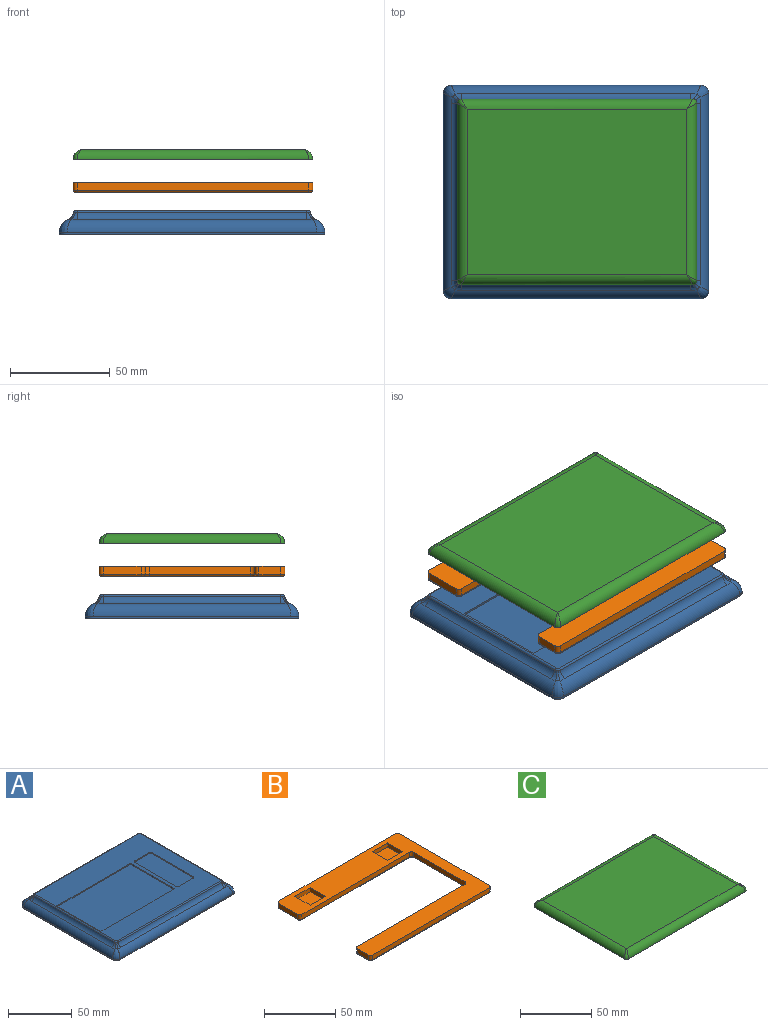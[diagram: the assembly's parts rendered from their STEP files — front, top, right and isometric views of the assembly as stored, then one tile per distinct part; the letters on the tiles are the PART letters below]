
ASSEMBLY  parts=3 mates=2
PART A: 56 faces, bbox 133x107x12 mm
  f0: plane 117x91mm, normal (0,0,1), area 5700.6mm2, adj f18,f19,f20,f21,f22,f23,f24,f25
  f1: plane 125x1mm, normal (0,1,0), area 125mm2, adj f5,f6,f9,f10
  f2: plane 99x1mm, normal (-1,0,0), area 99mm2, adj f5,f6,f7,f13
  f3: plane 125x1mm, normal (0,-1,0), area 125mm2, adj f5,f7,f8,f17
  f4: plane 99x1mm, normal (1,0,0), area 99mm2, adj f5,f8,f9,f14
  f5: plane 133x107mm, normal (0,0,-1), area 14217.3mm2, adj f1,f2,f3,f4,f6,f7,f8,f9
  f6: cylinder r=4mm len=4mm, axis (0,0,1), area 6.3mm2, adj f1,f2,f5,f11
  f7: cylinder r=4mm len=4mm, axis (0,0,-1), area 6.3mm2, adj f2,f3,f5,f15
  f8: cylinder r=4mm len=4mm, axis (0,0,1), area 6.3mm2, adj f3,f4,f5,f16
  f9: cylinder r=4mm len=4mm, axis (0,0,-1), area 6.3mm2, adj f1,f4,f5,f12
  f10: cylinder r=7mm len=125mm, axis (1,0,0), area 991mm2, adj f1,f11,f12,f39,f40,f41
  f11: bspline ~7.26x6.22mm, area 43.4mm2, adj f6,f10,f13,f37
  f12: bspline ~7.26x6.22mm, area 43.4mm2, adj f9,f10,f14,f38
  f13: cylinder r=7mm len=99mm, axis (0,1,0), area 782.1mm2, adj f2,f11,f15,f31,f33,f35
  f14: cylinder r=7mm len=99mm, axis (0,-1,0), area 782.1mm2, adj f4,f12,f16,f32,f34,f36
  f15: bspline ~7.26x6.22mm, area 43.4mm2, adj f7,f13,f17,f29
  f16: bspline ~7.26x6.22mm, area 43.4mm2, adj f8,f14,f17,f30
  f17: cylinder r=7mm len=125mm, axis (-1,0,0), area 991mm2, adj f3,f15,f16,f26,f27,f28
  f18: cylinder r=1mm len=115mm, axis (-1,0,0), area 162.5mm2, adj f0,f19,f20,f26
  f19: torus R=1mm, axis (0,0,1), area 3.4mm2, adj f0,f18,f21,f27,f29,f31
  f20: torus R=1mm, axis (0,0,1), area 3.4mm2, adj f0,f18,f22,f28,f30,f32
  f21: cylinder r=1mm len=89mm, axis (0,1,0), area 125.8mm2, adj f0,f19,f23,f33
  f22: cylinder r=1mm len=89mm, axis (0,-1,0), area 125.8mm2, adj f0,f20,f24,f34
  f23: torus R=1mm, axis (0,0,1), area 3.4mm2, adj f0,f21,f25,f35,f37,f39
  f24: torus R=1mm, axis (0,0,1), area 3.4mm2, adj f0,f22,f25,f36,f38,f40
  f25: cylinder r=1mm len=115mm, axis (1,0,0), area 162.5mm2, adj f0,f23,f24,f41
  f26: cylinder r=5mm len=115mm, axis (-1,0,0), area 569.3mm2, adj f17,f18,f27,f28
  f27: bspline ~5.33x3.88mm, area 9.5mm2, adj f17,f19,f26,f29
  f28: bspline ~5.12x3.85mm, area 9.5mm2, adj f17,f20,f26,f30
  f29: bspline ~3.88x3.85mm, area 7.1mm2, adj f15,f19,f27,f31
  f30: bspline ~3.9x3.82mm, area 7.1mm2, adj f16,f20,f28,f32
  f31: bspline ~5.33x3.88mm, area 9.5mm2, adj f13,f19,f29,f33
  f32: bspline ~5.33x3.88mm, area 9.5mm2, adj f14,f20,f30,f34
  f33: cylinder r=5mm len=89mm, axis (0,1,0), area 440.6mm2, adj f13,f21,f31,f35
  f34: cylinder r=5mm len=89mm, axis (0,1,0), area 440.6mm2, adj f14,f22,f32,f36
  f35: bspline ~5.33x3.88mm, area 9.5mm2, adj f13,f23,f33,f37
  f36: bspline ~5.12x3.85mm, area 9.5mm2, adj f14,f24,f34,f38
  f37: bspline ~3.9x3.82mm, area 7.1mm2, adj f11,f23,f35,f39
  f38: bspline ~3.88x3.85mm, area 7.1mm2, adj f12,f24,f36,f40
  f39: bspline ~5.33x3.88mm, area 9.5mm2, adj f10,f23,f37,f41
  f40: bspline ~5.33x3.88mm, area 9.5mm2, adj f10,f24,f38,f41
  f41: cylinder r=5mm len=115mm, axis (-1,0,0), area 569.3mm2, adj f10,f25,f39,f40
  f42: plane 45x1mm, normal (-1,0,0), area 45mm2, adj f0,f43,f49,f50
  f43: cylinder r=2mm len=2mm, axis (0,0,1), area 3.1mm2, adj f0,f42,f44,f50
  f44: plane 15x1mm, normal (0,-1,0), area 15mm2, adj f0,f43,f45,f50
  f45: cylinder r=2mm len=2mm, axis (0,0,1), area 3.1mm2, adj f0,f44,f46,f50
  f46: plane 45x1mm, normal (1,0,0), area 45mm2, adj f0,f45,f47,f50
  f47: cylinder r=2mm len=2mm, axis (0,0,1), area 3.1mm2, adj f0,f46,f48,f50
  f48: plane 15x1mm, normal (0,1,0), area 15mm2, adj f0,f47,f49,f50
  f49: cylinder r=2mm len=2mm, axis (0,0,1), area 3.1mm2, adj f0,f42,f48,f50
  f50: plane 49x19mm, normal (0,0,1), area 927.6mm2, adj f42,f43,f44,f45,f46,f47,f48,f49
  f51: plane 82x1mm, normal (0,-1,0), area 82mm2, adj f0,f52,f54,f55
  f52: plane 49x1mm, normal (1,0,0), area 49mm2, adj f0,f51,f53,f55
  f53: plane 82x1mm, normal (0,1,0), area 82mm2, adj f0,f52,f54,f55
  f54: plane 49x1mm, normal (-1,0,0), area 49mm2, adj f0,f51,f53,f55
  f55: plane 82x49mm, normal (0,0,1), area 4018mm2, adj f51,f52,f53,f54
PART B: 44 faces, bbox 120.3x93.3x5 mm
  f0: plane 120x93mm, normal (0,0,1), area 4601.6mm2, adj f1,f2,f3,f4,f5,f6,f7,f8
  f1: cylinder r=2mm len=4mm, axis (0,0,-1), area 12.6mm2, adj f0,f2,f16,f42
  f2: plane 51x4mm, normal (-1,0,0), area 204mm2, adj f0,f1,f3,f40
  f3: cylinder r=2mm len=4mm, axis (0,0,-1), area 12.6mm2, adj f0,f2,f4,f38
  f4: plane 107x4mm, normal (0,1,0), area 428mm2, adj f0,f3,f5,f36
  f5: cylinder r=2mm len=4mm, axis (0,0,-1), area 12.6mm2, adj f0,f4,f6,f34
  f6: plane 11x4mm, normal (-1,0,0), area 44mm2, adj f0,f5,f7,f32
  f7: cylinder r=2mm len=4mm, axis (0,0,-1), area 12.6mm2, adj f0,f6,f8,f30
  f8: plane 116x4mm, normal (0,-1,0), area 464mm2, adj f0,f7,f9,f28
  f9: cylinder r=2mm len=4mm, axis (0,0,-1), area 12.6mm2, adj f0,f8,f10,f29
  f10: plane 89x4mm, normal (1,0,0), area 356mm2, adj f0,f9,f11,f31
  f11: cylinder r=2mm len=4mm, axis (0,0,-1), area 12.6mm2, adj f0,f10,f12,f33
  f12: plane 116x4mm, normal (0,1,0), area 464mm2, adj f0,f11,f13,f35
  f13: cylinder r=2mm len=4mm, axis (0,0,-1), area 12.6mm2, adj f0,f12,f14,f37
  f14: plane 19x4mm, normal (-1,0,0), area 76mm2, adj f0,f13,f15,f39
  f15: cylinder r=2mm len=4mm, axis (0,0,-1), area 12.6mm2, adj f0,f14,f16,f41
  f16: plane 107x4mm, normal (0,-1,0), area 428mm2, adj f0,f1,f15,f43
  f17: plane 118x91mm, normal (0,0,-1), area 4413.6mm2, adj f28,f29,f30,f31,f32,f33,f34,f35
  f18: plane 15x3.5mm, normal (0,-1,0), area 52.5mm2, adj f0,f19,f21,f22
  f19: plane 15x3.5mm, normal (1,0,0), area 52.5mm2, adj f0,f18,f20,f22
  f20: plane 15x3.5mm, normal (0,1,0), area 52.5mm2, adj f0,f19,f21,f22
  f21: plane 15x3.5mm, normal (-1,0,0), area 52.5mm2, adj f0,f18,f20,f22
  f22: plane 15x15mm, normal (0,0,1), area 225mm2, adj f18,f19,f20,f21
  f23: plane 15x3.5mm, normal (0,-1,0), area 52.5mm2, adj f0,f24,f26,f27
  f24: plane 15x3.5mm, normal (1,0,0), area 52.5mm2, adj f0,f23,f25,f27
  f25: plane 15x3.5mm, normal (0,1,0), area 52.5mm2, adj f0,f24,f26,f27
  f26: plane 15x3.5mm, normal (-1,0,0), area 52.5mm2, adj f0,f23,f25,f27
  f27: plane 15x15mm, normal (0,0,1), area 225mm2, adj f23,f24,f25,f26
  f28: cylinder r=1mm len=116mm, axis (1,0,0), area 182.2mm2, adj f8,f17,f29,f30
  f29: torus R=1mm, axis (0,0,1), area 4mm2, adj f9,f17,f28,f31
  f30: torus R=1mm, axis (0,0,1), area 4mm2, adj f7,f17,f28,f32
  f31: cylinder r=1mm len=89mm, axis (0,1,0), area 139.8mm2, adj f10,f17,f29,f33
  f32: cylinder r=1mm len=11mm, axis (0,-1,0), area 17.3mm2, adj f6,f17,f30,f34
  f33: torus R=1mm, axis (0,0,1), area 4mm2, adj f11,f17,f31,f35
  f34: torus R=1mm, axis (0,0,1), area 4mm2, adj f5,f17,f32,f36
  f35: cylinder r=1mm len=116mm, axis (-1,0,0), area 182.2mm2, adj f12,f17,f33,f37
  f36: cylinder r=1mm len=107mm, axis (-1,0,0), area 168.1mm2, adj f4,f17,f34,f38
  f37: torus R=1mm, axis (0,0,1), area 4mm2, adj f13,f17,f35,f39
  f38: torus R=3mm, axis (0,0,1), area 5.8mm2, adj f3,f17,f36,f40
  f39: cylinder r=1mm len=19mm, axis (0,-1,0), area 29.8mm2, adj f14,f17,f37,f41
  f40: cylinder r=1mm len=51mm, axis (0,-1,0), area 80.1mm2, adj f2,f17,f38,f42
  f41: torus R=1mm, axis (0,0,1), area 4mm2, adj f15,f17,f39,f43
  f42: torus R=3mm, axis (0,0,1), area 5.8mm2, adj f1,f17,f40,f43
  f43: cylinder r=1mm len=107mm, axis (1,0,0), area 168.1mm2, adj f16,f17,f41,f42
PART C: 20 faces, bbox 120x93x5.9 mm
  f0: plane 120x93mm, normal (0,0,-1), area 10706.6mm2, adj f2,f3,f4,f5,f6,f7,f8,f9
  f1: plane 110x83mm, normal (0,0,1), area 9130mm2, adj f2,f5,f6,f9
  f2: cylinder r=5mm len=116mm, axis (1,0,0), area 893.9mm2, adj f0,f1,f3,f4
  f3: bspline ~5.91x5mm, area 16.7mm2, adj f0,f2,f5
  f4: bspline ~5.91x5mm, area 16.7mm2, adj f0,f2,f6
  f5: cylinder r=5mm len=89mm, axis (0,1,0), area 681.9mm2, adj f0,f1,f3,f7
  f6: cylinder r=5mm len=89mm, axis (0,-1,0), area 681.9mm2, adj f0,f1,f4,f8
  f7: bspline ~5.91x5mm, area 16.7mm2, adj f0,f5,f9
  f8: bspline ~5.91x5mm, area 16.7mm2, adj f0,f6,f9
  f9: cylinder r=5mm len=116mm, axis (-1,0,0), area 893.9mm2, adj f0,f1,f7,f8
  f10: plane 15x3.5mm, normal (0,-1,0), area 52.5mm2, adj f0,f11,f13,f14
  f11: plane 15x3.5mm, normal (-1,0,0), area 52.5mm2, adj f0,f10,f12,f14
  f12: plane 15x3.5mm, normal (0,1,0), area 52.5mm2, adj f0,f11,f13,f14
  f13: plane 15x3.5mm, normal (1,0,0), area 52.5mm2, adj f0,f10,f12,f14
  f14: plane 15x15mm, normal (0,0,-1), area 225mm2, adj f10,f11,f12,f13
  f15: plane 15x3.5mm, normal (0,-1,0), area 52.5mm2, adj f0,f16,f18,f19
  f16: plane 15x3.5mm, normal (-1,0,0), area 52.5mm2, adj f0,f15,f17,f19
  f17: plane 15x3.5mm, normal (0,1,0), area 52.5mm2, adj f0,f16,f18,f19
  f18: plane 15x3.5mm, normal (1,0,0), area 52.5mm2, adj f0,f15,f17,f19
  f19: plane 15x15mm, normal (0,0,-1), area 225mm2, adj f15,f16,f17,f18
PLACE A t=(-32.55,61.87,-30.78)mm
PLACE B t=(-25.55,54.87,-9.6)mm
PLACE C t=(-25.55,54.87,6.8)mm
MATE slider B.f17 <-> A.f0  axis (0,0,-1) through (-23.55,53.87,-9.6)mm
MATE slider C.f0 <-> B.f0  axis (0,0,-1) through (-23.55,54.87,6.8)mm
